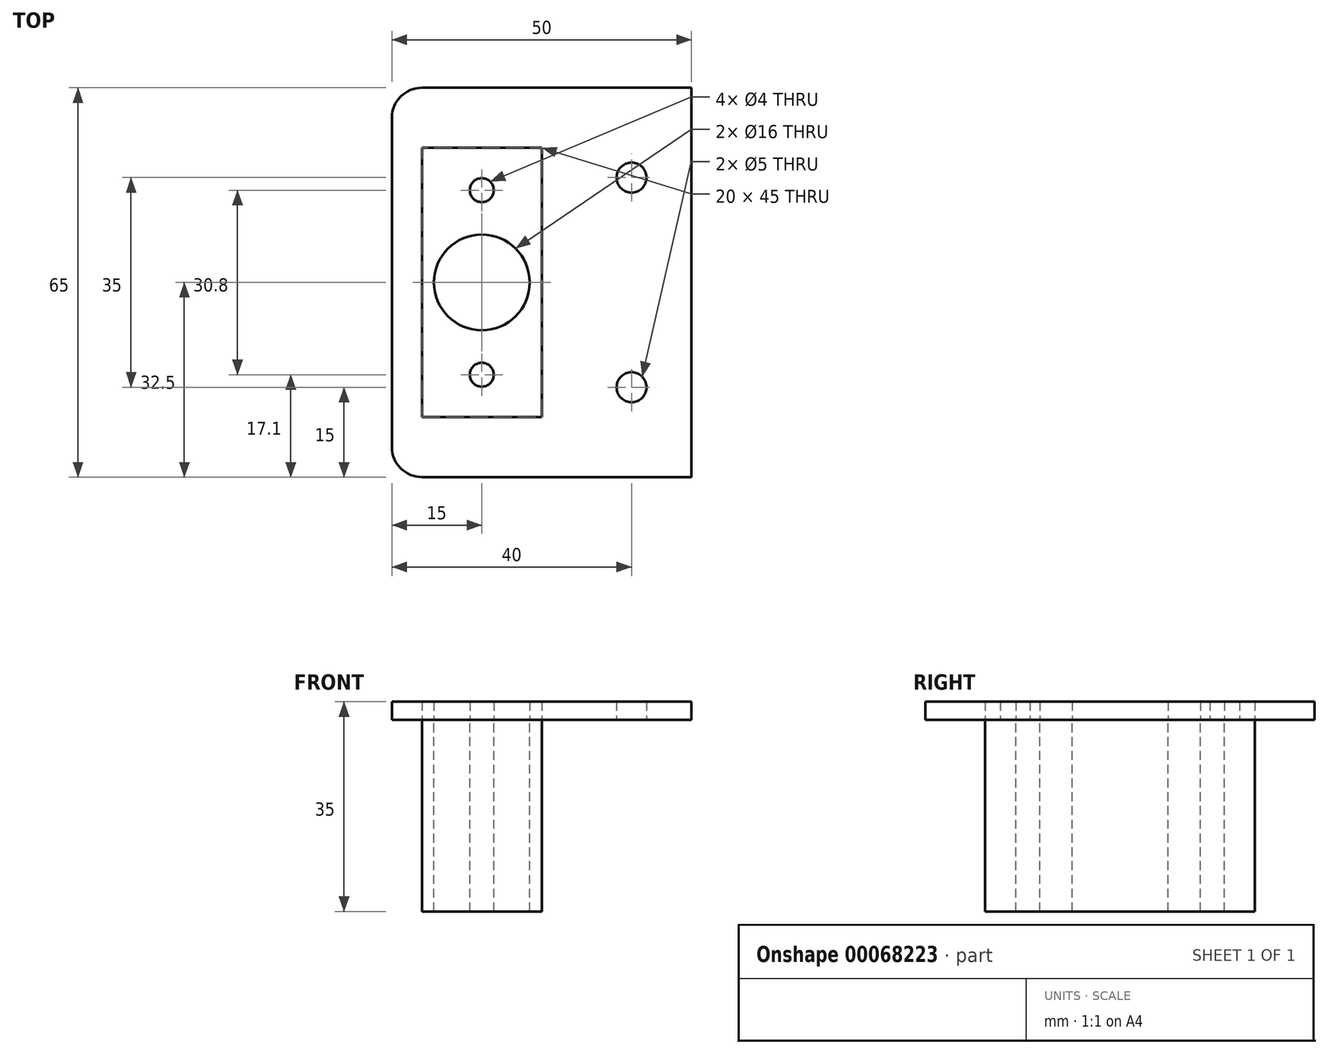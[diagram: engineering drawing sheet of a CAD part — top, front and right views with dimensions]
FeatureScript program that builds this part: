
annotation { "Feature Type Name" : "Feature", "Feature Type Description" : "" }
export const myFeature = defineFeature(function(context is Context, id is Id, definition is map)
    precondition{}
    {
        {
            var Q0;
            Q0=qCreatedBy(makeId("Top.planeOp"),FACE);
            var sketch = newSketch(context, id + "F0", { "sketchPlane" : qUnion([Q0])});
            skLineSegment(sketch, "E0.bottom", {"start": v(-10, 22.5) * mm, "end": v(10, 22.5) * mm});
            skLineSegment(sketch, "E0.top", {"start": v(-10, -22.5) * mm, "end": v(10, -22.5) * mm});
            skLineSegment(sketch, "E0.left", {"start": v(-10, 22.5) * mm, "end": v(-10, -22.5) * mm});
            skLineSegment(sketch, "E0.right", {"start": v(10, 22.5) * mm, "end": v(10, -22.5) * mm});
            skPoint(sketch, "E0.middle", {"position": v(0, 0) * mm});
            skCircle(sketch, "E1", {"center": v(0, 0) * mm, "radius": 8 * mm});
            skCircle(sketch, "E2", {"center": v(0, 15.4) * mm, "radius": 2 * mm});
            skCircle(sketch, "E3.MirrorC", {"center": v(0, -15.4) * mm, "radius": 2 * mm});
            skSolve(sketch);
        }
        {
            var Q0;
            Q0 = qSketchRegion(id + "F0", true);
            extrude(context, id + "F1", {"entities" : qUnion([Q0]), "oppositeDirection" : true, "depth" : 32 * mm});
        }
        {
            var Q0;
            Q0=makeQuery(id+"F0.imprint","IMPRINT",FACE,{"disambiguationData":[TD([[makeQuery(id+"F0.imprint","IMPRINT",EDGE,{"derivedFrom":sQuery(id+"F0.wireOp",EDGE,"E1")}),1.0]])]});
            extrude(context, id + "F2", {"entities" : qUnion([Q0]), "depth" : 3 * mm});
        }
        {
            var Q0;
            Q0=makeQuery(id+"F0.imprint","IMPRINT",FACE,{"disambiguationData":[TD([[makeQuery(id+"F0.imprint","IMPRINT",EDGE,{"derivedFrom":sQuery(id+"F0.wireOp",EDGE,"E0.bottom")}),-1.0]])]});
            var sketch = newSketch(context, id + "F3", { "sketchPlane" : qUnion([Q0])});
            skLineSegment(sketch, "E4.bottom", {"start": v(15, 32.5) * mm, "end": v(-15, 32.5) * mm});
            skLineSegment(sketch, "E4.top", {"start": v(15, -32.5) * mm, "end": v(-15, -32.5) * mm});
            skLineSegment(sketch, "E4.left", {"start": v(15, 32.5) * mm, "end": v(15, -32.5) * mm});
            skLineSegment(sketch, "E4.right", {"start": v(-15, 32.5) * mm, "end": v(-15, -32.5) * mm});
            skPoint(sketch, "E4.middle", {"position": v(0, 0) * mm});
            skLineSegment(sketch, "E5.bottom", {"start": v(15, 32.5) * mm, "end": v(35, 32.5) * mm});
            skLineSegment(sketch, "E5.top", {"start": v(15, -32.5) * mm, "end": v(35, -32.5) * mm});
            skLineSegment(sketch, "E5.right", {"start": v(35, 32.5) * mm, "end": v(35, -32.5) * mm});
            skLineSegment(sketch, "E6", {"start": v(25, 32.5) * mm, "end": v(25, -32.5) * mm, "construction": true});
            skCircle(sketch, "E7", {"center": v(25, 17.5) * mm, "radius": 2.5 * mm});
            skLineSegment(sketch, "E8.MirrorCS", {"start": v(25, -32.5) * mm, "end": v(25, 32.5) * mm, "construction": true});
            skCircle(sketch, "E9.MirrorC", {"center": v(25, -17.5) * mm, "radius": 2.5 * mm});
            skCircle(sketch, "E10", {"center": v(0, 15.48) * mm, "radius": 2 * mm});
            skCircle(sketch, "E11.MirrorC", {"center": v(0, -15.48) * mm, "radius": 2 * mm});
            skCircle(sketch, "E12", {"center": v(0, 0) * mm, "radius": 7.44 * mm});
            skSolve(sketch);
        }
        {
            var Q0;
            Q0=makeQuery(id+"F3.imprint","IMPRINT",FACE,{"disambiguationData":[TD([[makeQuery(id+"F3.imprint","IMPRINT",EDGE,{"derivedFrom":sQuery(id+"F3.wireOp",EDGE,"E4.bottom")}),1.0]])]});
            var Q1;
            Q1=makeQuery(id+"F3.imprint","IMPRINT",FACE,{"disambiguationData":[TD([[makeQuery(id+"F3.imprint","IMPRINT",EDGE,{"derivedFrom":sQuery(id+"F3.wireOp",EDGE,"E5.bottom")}),-1.0]])]});
            var Q2;
            Q2=makeQuery(id+"F0.imprint","IMPRINT",FACE,{"disambiguationData":[TD([[makeQuery(id+"F0.imprint","IMPRINT",EDGE,{"derivedFrom":sQuery(id+"F0.wireOp",EDGE,"E0.bottom")}),-1.0]])]});
            extrude(context, id + "F4", {"entities" : qUnion([Q0, Q1, Q2]), "depth" : 3 * mm});
        }
        {
            var Q0;
            Q0=makeQuery(id+"F4.opExtrude","SWEPT_EDGE",EDGE,{"disambiguationData":[OSD([sQuery(id+"F3.wireOp",EDGE,"E4.bottom"),sQuery(id+"F3.wireOp",EDGE,"E4.right")])]});
            var Q1;
            Q1=makeQuery(id+"F4.opExtrude","SWEPT_EDGE",EDGE,{"disambiguationData":[OSD([sQuery(id+"F3.wireOp",EDGE,"E4.top"),sQuery(id+"F3.wireOp",EDGE,"E4.right")])]});
            fillet(context, id + "F5", {"entities" : qUnion([Q0, Q1]), "radius" : 5 * mm, "tangentPropagation" : true, "allowEdgeOverflow" : false});
        }
    });
